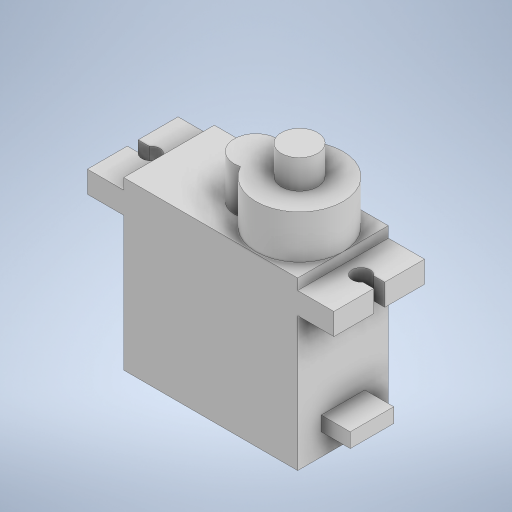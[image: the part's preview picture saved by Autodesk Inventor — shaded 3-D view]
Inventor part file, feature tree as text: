
AUTODESK INVENTOR PART (.ipt)
format: ipt  version: 2023 (Build 270158000, 158)  size: 308,224 bytes
history: native  units: mm
features: extrude x5, sketch x5, projected_geometry x2, other x1
ambient origin geometry x8: Origin, YZ Plane, XZ Plane, XY Plane, X Axis, Y Axis, Z Axis, Center Point
bodies: Body1 (feature_tree)
feature tree (13):
  other  "實體1"
  extrude  "擠出1"  Depth=24.0mm
  extrude  "擠出2"  Depth=18.5mm
  extrude  "擠出3"  Depth=34.0mm
  extrude  "擠出4"  Depth=3.0mm
  extrude  "擠出5"  Depth=1.5mm
  sketch  "草圖1"
  sketch  "草圖2"
  sketch  "草圖3"
  sketch  "草圖4"
  projected_geometry  "投影迴路1"
  sketch  "草圖5"
  projected_geometry  "投影迴路2"
